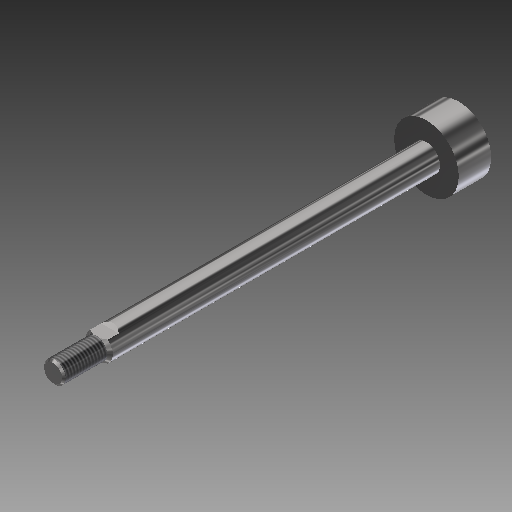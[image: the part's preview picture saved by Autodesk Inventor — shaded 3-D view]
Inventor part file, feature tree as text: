
AUTODESK INVENTOR PART (.ipt)
format: ipt  version: 2018 (Build 220112000, 112)  size: 146,944 bytes
history: native  units: in
note: dims shown in document units (in); Inventor stores cm internally (conversion verified against a paired STEP export)
features: other x7, sketch x3, extrude x2, revolve x1, thread x1
ambient origin geometry x8: Origin, YZ Plane, XZ Plane, XY Plane, X Axis, Y Axis, Z Axis, Center Point
bodies: Solid1 (feature_tree)
feature tree (14):
  revolve  "Revolution1"  [1 undecoded]
  thread  "Thread1"  [1 undecoded]
  extrude  "Extrusion1"  TaperAngle=0.0deg  [1 undecoded]
  extrude  "Extrusion2"  [1 undecoded]
  other  "conn_XY"
  other  "conn_YZ"
  other  "conn_ZX"
  other  "conn_X"
  other  "conn_Y"
  other  "conn_Z"
  other  "conn_Center"
  sketch  "Sketch_1"  dims[d0=360.0deg d1=0.4787in d2=0.0in d3=0.63in d4=0.0in]
  sketch  "Sketch_2"  dims[d5=0.63in d6=0.0in d7=0.0in]
  sketch  "Sketch_3"
note: 4 required parameter values undecoded (feature->parameter linkage not recoverable at this tier; creation-order binding heuristic only, values carry confidence <= 0.55)